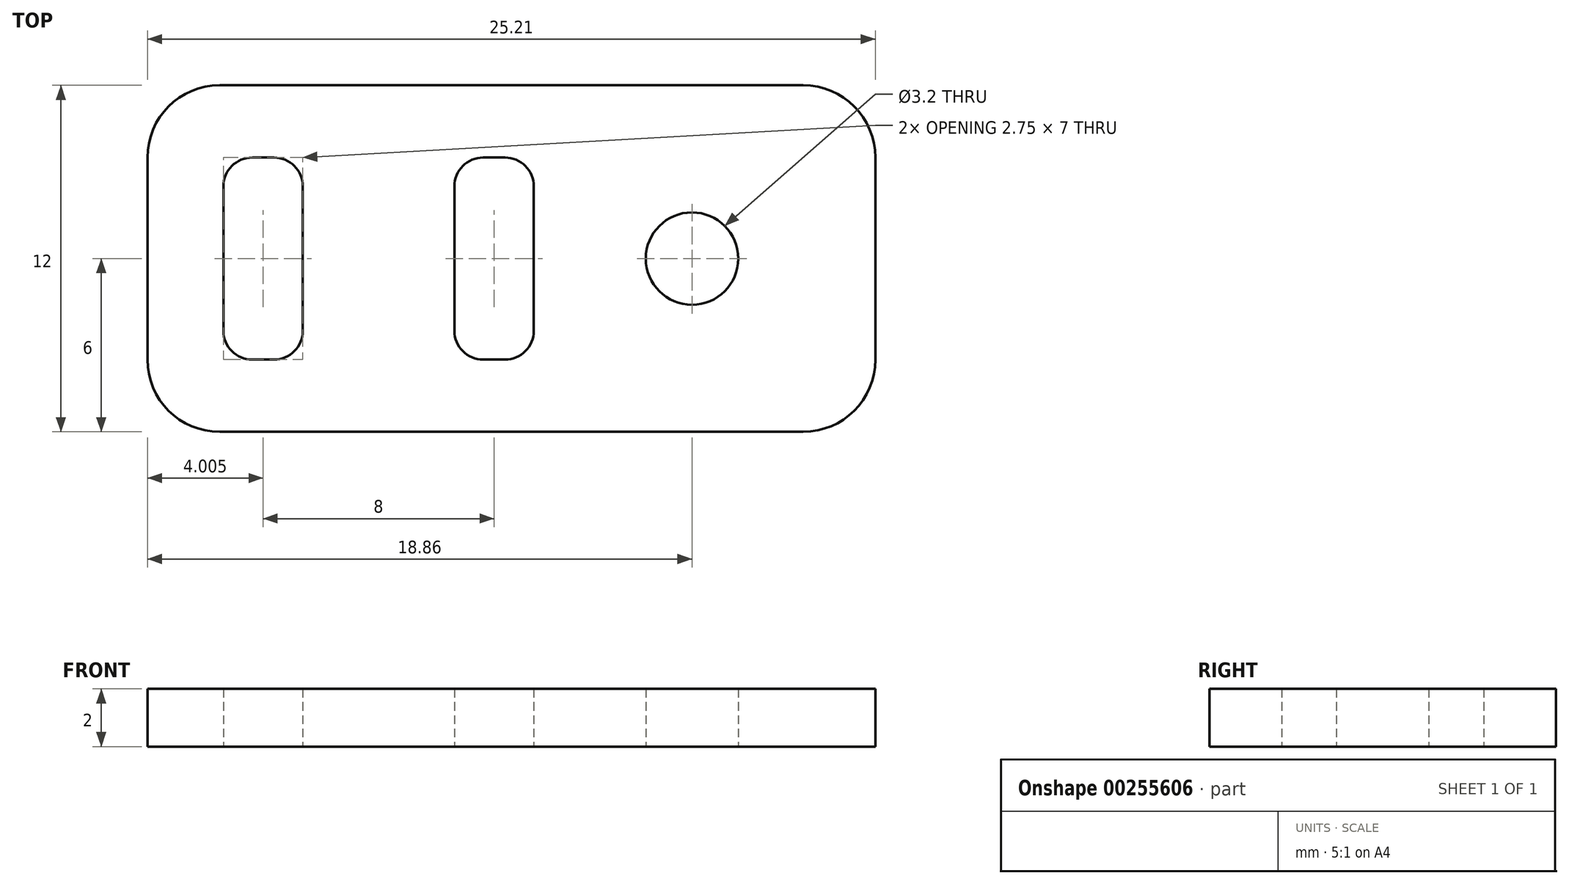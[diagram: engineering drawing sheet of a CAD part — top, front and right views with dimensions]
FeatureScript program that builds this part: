
annotation { "Feature Type Name" : "Feature", "Feature Type Description" : "" }
export const myFeature = defineFeature(function(context is Context, id is Id, definition is map)
    precondition{}
    {
        {
            var Q0;
            Q0=qCreatedBy(makeId("Top.planeOp"),FACE);
            var sketch = newSketch(context, id + "F0", { "sketchPlane" : qUnion([Q0])});
            skCircle(sketch, "E0", {"center": v(0, 0) * mm, "radius": 1.6 * mm});
            skLineSegment(sketch, "E1.bottom", {"start": v(-16.36, 6) * mm, "end": v(3.85, 6) * mm});
            skLineSegment(sketch, "E1.top", {"start": v(-16.36, -6) * mm, "end": v(3.85, -6) * mm});
            skLineSegment(sketch, "E1.left", {"start": v(-18.86, 3.5) * mm, "end": v(-18.86, -3.5) * mm});
            skLineSegment(sketch, "E1.right", {"start": v(6.35, 3.5) * mm, "end": v(6.35, -3.5) * mm});
            skLineSegment(sketch, "E2.bottom", {"start": v(-15.23, 3.5) * mm, "end": v(-14.48, 3.5) * mm});
            skLineSegment(sketch, "E2.top", {"start": v(-15.23, -3.5) * mm, "end": v(-14.48, -3.5) * mm});
            skLineSegment(sketch, "E2.left", {"start": v(-16.23, 2.5) * mm, "end": v(-16.23, -2.5) * mm});
            skLineSegment(sketch, "E2.right", {"start": v(-13.48, 2.5) * mm, "end": v(-13.48, -2.5) * mm});
            skLineSegment(sketch, "E3.bottom", {"start": v(-7.23, 3.5) * mm, "end": v(-6.48, 3.5) * mm});
            skLineSegment(sketch, "E3.top", {"start": v(-7.23, -3.5) * mm, "end": v(-6.48, -3.5) * mm});
            skLineSegment(sketch, "E3.left", {"start": v(-8.23, 2.5) * mm, "end": v(-8.23, -2.5) * mm});
            skLineSegment(sketch, "E3.right", {"start": v(-5.48, 2.5) * mm, "end": v(-5.48, -2.5) * mm});
            skPoint(sketch, "E4.visualSharp", {"position": v(-16.23, 3.5) * mm});
            skArc(sketch, "E4.filletArc", {"start": v(-15.23, 3.5) * mm, "mid": v(-15.94, 3.2) * mm, "end": v(-16.23, 2.5) * mm});
            skPoint(sketch, "E5.visualSharp", {"position": v(-16.23, -3.5) * mm});
            skArc(sketch, "E5.filletArc", {"start": v(-16.23, -2.5) * mm, "mid": v(-15.94, -3.2) * mm, "end": v(-15.23, -3.5) * mm});
            skPoint(sketch, "E6.visualSharp", {"position": v(-13.48, -3.5) * mm});
            skArc(sketch, "E6.filletArc", {"start": v(-14.48, -3.5) * mm, "mid": v(-13.77, -3.2) * mm, "end": v(-13.48, -2.5) * mm});
            skPoint(sketch, "E7.visualSharp", {"position": v(-13.48, 3.5) * mm});
            skArc(sketch, "E7.filletArc", {"start": v(-13.48, 2.5) * mm, "mid": v(-13.77, 3.2) * mm, "end": v(-14.48, 3.5) * mm});
            skPoint(sketch, "E8.visualSharp", {"position": v(-8.23, 3.5) * mm});
            skArc(sketch, "E8.filletArc", {"start": v(-7.23, 3.5) * mm, "mid": v(-7.94, 3.2) * mm, "end": v(-8.23, 2.5) * mm});
            skPoint(sketch, "E9.visualSharp", {"position": v(-8.23, -3.5) * mm});
            skArc(sketch, "E9.filletArc", {"start": v(-8.23, -2.5) * mm, "mid": v(-7.94, -3.2) * mm, "end": v(-7.23, -3.5) * mm});
            skPoint(sketch, "E10.visualSharp", {"position": v(-5.48, -3.5) * mm});
            skArc(sketch, "E10.filletArc", {"start": v(-6.48, -3.5) * mm, "mid": v(-5.77, -3.2) * mm, "end": v(-5.48, -2.5) * mm});
            skPoint(sketch, "E11.visualSharp", {"position": v(-5.48, 3.5) * mm});
            skArc(sketch, "E11.filletArc", {"start": v(-5.48, 2.5) * mm, "mid": v(-5.77, 3.2) * mm, "end": v(-6.48, 3.5) * mm});
            skPoint(sketch, "E12.visualSharp", {"position": v(-18.86, 6) * mm});
            skArc(sketch, "E12.filletArc", {"start": v(-16.36, 6) * mm, "mid": v(-18.13, 5.27) * mm, "end": v(-18.86, 3.5) * mm});
            skPoint(sketch, "E13.visualSharp", {"position": v(-18.86, -6) * mm});
            skArc(sketch, "E13.filletArc", {"start": v(-18.86, -3.5) * mm, "mid": v(-18.13, -5.27) * mm, "end": v(-16.36, -6) * mm});
            skPoint(sketch, "E14.visualSharp", {"position": v(6.35, -6) * mm});
            skArc(sketch, "E14.filletArc", {"start": v(3.85, -6) * mm, "mid": v(5.62, -5.27) * mm, "end": v(6.35, -3.5) * mm});
            skPoint(sketch, "E15.visualSharp", {"position": v(6.35, 6) * mm});
            skArc(sketch, "E15.filletArc", {"start": v(6.35, 3.5) * mm, "mid": v(5.62, 5.27) * mm, "end": v(3.85, 6) * mm});
            skSolve(sketch);
        }
        {
            var Q0;
            Q0 = qSketchRegion(id + "F0", true);
            extrude(context, id + "F1", {"entities" : qUnion([Q0]), "depth" : 2 * mm});
        }
    });
